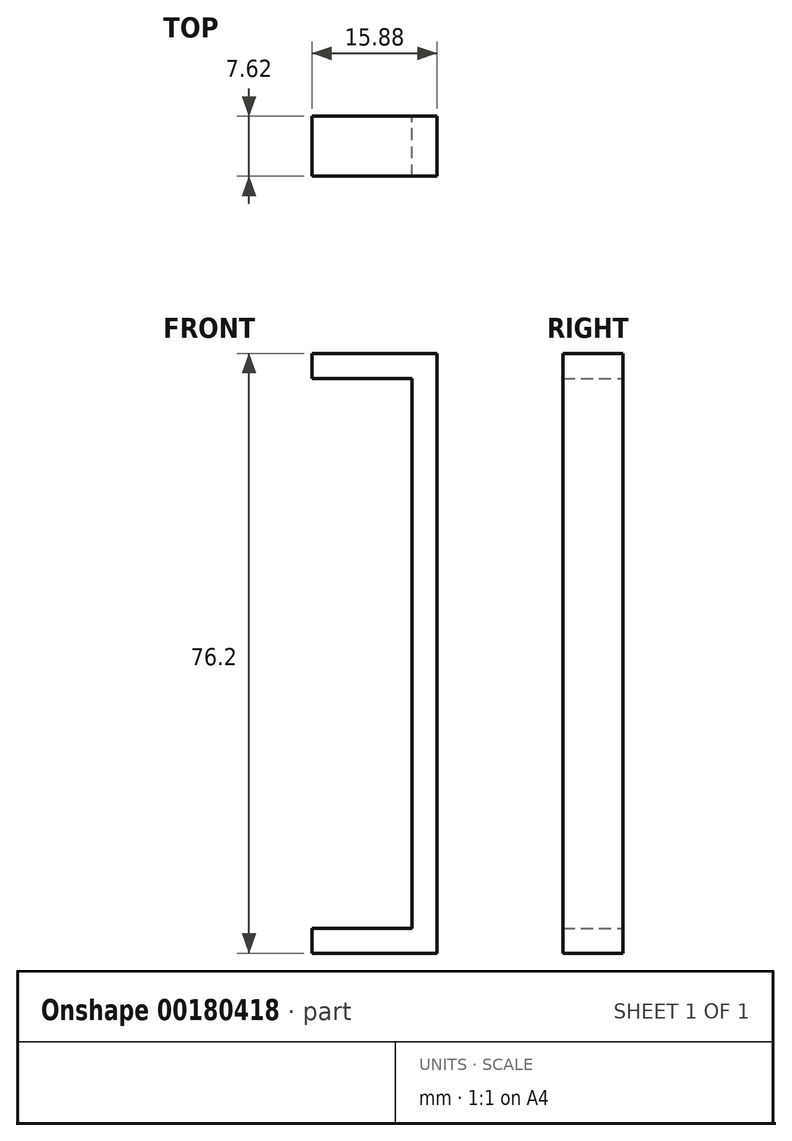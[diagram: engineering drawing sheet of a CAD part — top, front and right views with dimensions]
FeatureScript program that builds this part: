
annotation { "Feature Type Name" : "Feature", "Feature Type Description" : "" }
export const myFeature = defineFeature(function(context is Context, id is Id, definition is map)
    precondition{}
    {
        {
            var Q0;
            Q0=qCreatedBy(makeId("Front.planeOp"),FACE);
            var sketch = newSketch(context, id + "F0", { "sketchPlane" : qUnion([Q0])});
            skLineSegment(sketch, "E0", {"start": v(0, 0) * mm, "end": v(0, 3.17) * mm});
            skLineSegment(sketch, "E1", {"start": v(0, 3.17) * mm, "end": v(12.7, 3.17) * mm});
            skLineSegment(sketch, "E2", {"start": v(12.7, 3.18) * mm, "end": v(12.7, 73.03) * mm});
            skLineSegment(sketch, "E3", {"start": v(12.7, 73.03) * mm, "end": v(0, 73.03) * mm});
            skLineSegment(sketch, "E4", {"start": v(0, 73.03) * mm, "end": v(0, 76.2) * mm});
            skLineSegment(sketch, "E5", {"start": v(0, 76.2) * mm, "end": v(15.87, 76.2) * mm});
            skLineSegment(sketch, "E6", {"start": v(15.87, 76.2) * mm, "end": v(15.88, 0) * mm});
            skLineSegment(sketch, "E7", {"start": v(15.88, 0) * mm, "end": v(0, 0) * mm});
            skSolve(sketch);
        }
        {
            var Q0;
            Q0=makeQuery(id+"F0.imprint","IMPRINT",FACE,{"disambiguationData":[TD([[makeQuery(id+"F0.imprint","IMPRINT",EDGE,{"derivedFrom":sQuery(id+"F0.wireOp",EDGE,"E0")}),-1.0]])]});
            extrude(context, id + "F1", {"entities" : qUnion([Q0]), "depth" : 7.62 * mm});
        }
    });
